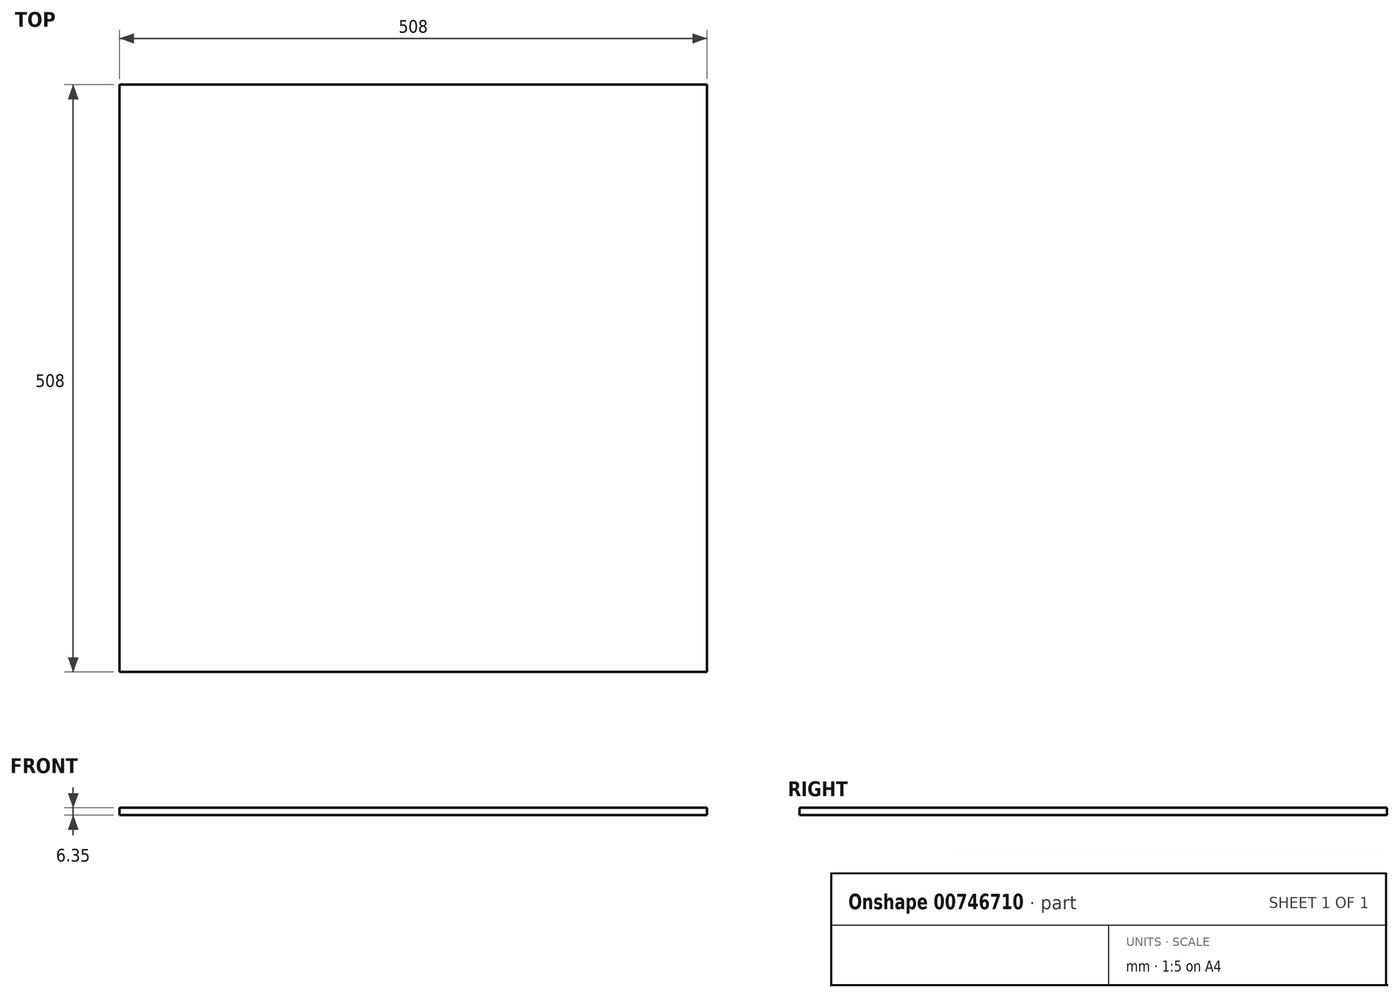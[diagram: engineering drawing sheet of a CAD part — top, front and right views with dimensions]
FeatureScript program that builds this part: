
annotation { "Feature Type Name" : "Feature", "Feature Type Description" : "" }
export const myFeature = defineFeature(function(context is Context, id is Id, definition is map)
    precondition{}
    {
        {
            var Q0;
            Q0=qCreatedBy(makeId("Top.planeOp"),FACE);
            var sketch = newSketch(context, id + "F0", { "sketchPlane" : qUnion([Q0])});
            skLineSegment(sketch, "E0.bottom", {"start": v(-272.82, -248.95) * mm, "end": v(235.18, -248.95) * mm});
            skLineSegment(sketch, "E0.top", {"start": v(-272.82, 259.05) * mm, "end": v(235.18, 259.05) * mm});
            skLineSegment(sketch, "E0.left", {"start": v(-272.82, -248.95) * mm, "end": v(-272.82, 259.05) * mm});
            skLineSegment(sketch, "E0.right", {"start": v(235.18, -248.95) * mm, "end": v(235.18, 259.05) * mm});
            skSolve(sketch);
        }
        {
            var Q0;
            Q0=qSketchRegion(id+"F0",true);
            extrude(context, id + "F1", {"entities" : qUnion([Q0]), "depth" : 6.35 * mm, "offsetDistance" : 25.4 * mm});
        }
        {
            var Q0;
            Q0=sQuery(id+"F0.wireOp",EDGE,"E0.bottom");
            var Q1;
            Q1=sQuery(id+"F0.wireOp",EDGE,"E0.right");
            var Q2;
            Q2=sQuery(id+"F0.wireOp",EDGE,"E0.top");
            var Q3;
            Q3=sQuery(id+"F0.wireOp",EDGE,"E0.left");
            extrude(context, id + "F2", {"bodyType" : ToolBodyType.SURFACE, "surfaceEntities" : qUnion([Q0, Q1, Q2, Q3]), "depth" : 25.4 * mm, "offsetDistance" : 25.4 * mm});
        }
    });
